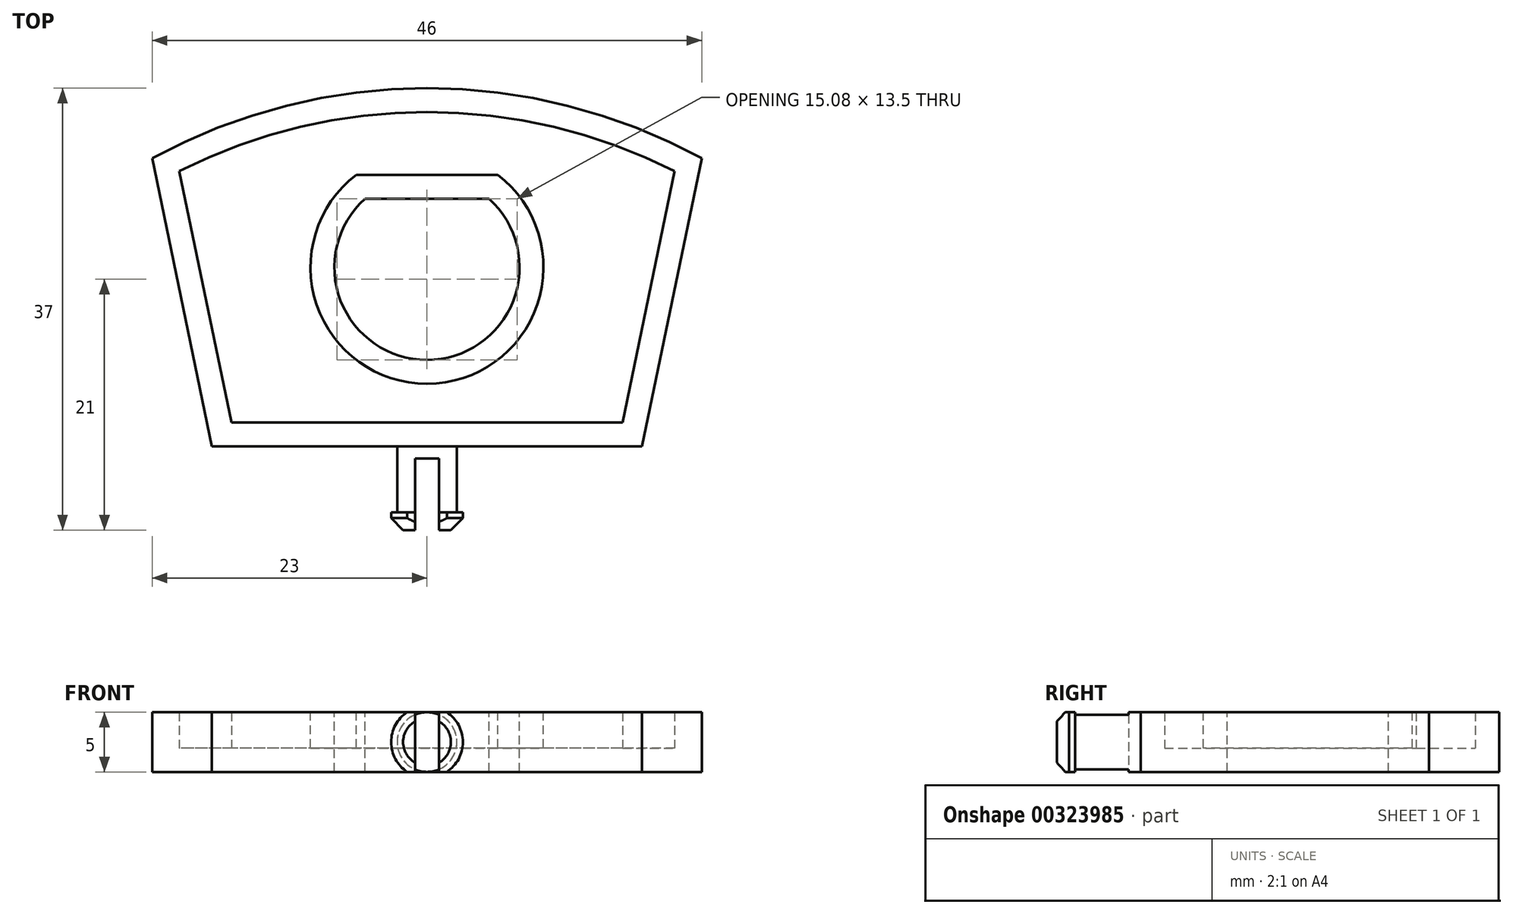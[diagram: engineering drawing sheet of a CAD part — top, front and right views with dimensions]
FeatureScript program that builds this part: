
annotation { "Feature Type Name" : "Feature", "Feature Type Description" : "" }
export const myFeature = defineFeature(function(context is Context, id is Id, definition is map)
    precondition{}
    {
        {
            var Q0;
            Q0=qCreatedBy(makeId("Top.planeOp"),FACE);
            var sketch = newSketch(context, id + "F0", { "sketchPlane" : qUnion([Q0])});
            skLineSegment(sketch, "E0", {"start": v(0, 0) * mm, "end": v(-18, 0) * mm});
            skLineSegment(sketch, "E1", {"start": v(-18, 0) * mm, "end": v(18, 0) * mm});
            skLineSegment(sketch, "E2", {"start": v(18, 0) * mm, "end": v(23, 24.13) * mm});
            skLineSegment(sketch, "E3", {"start": v(23, 24.13) * mm, "end": v(18, 0) * mm});
            skLineSegment(sketch, "E4", {"start": v(-18, 0) * mm, "end": v(-23, 24.13) * mm});
            skArc(sketch, "E5", {"start": v(23, 24.13) * mm, "mid": v(0, 30) * mm, "end": v(-23, 24.13) * mm});
            skSolve(sketch);
        }
        {
            var Q0;
            Q0 = qSketchRegion(id + "F0", true);
            extrude(context, id + "F1", {"entities" : qUnion([Q0]), "endBound" : BoundingType.SYMMETRIC, "depth" : 5 * mm});
        }
        {
            var Q0;
            Q0=makeQuery(id+"F1.opExtrude","CAP_FACE",FACE,{"disambiguationData":[OSD([sQuery(id+"F0.wireOp",EDGE,"E1"),sQuery(id+"F0.wireOp",EDGE,"E3"),sQuery(id+"F0.wireOp",EDGE,"E4"),sQuery(id+"F0.wireOp",EDGE,"E5")])],"isStart":false});
            var sketch = newSketch(context, id + "F2", { "sketchPlane" : qUnion([Q0])});
            skLineSegment(sketch, "E6", {"start": v(-5.2, 20.75) * mm, "end": v(5.2, 20.75) * mm});
            skArc(sketch, "E7", {"start": v(-5.2, 20.75) * mm, "mid": v(0, 7.25) * mm, "end": v(5.2, 20.75) * mm});
            skSolve(sketch);
        }
        {
            var Q0;
            Q0 = qSketchRegion(id + "F2", true);
            extrude(context, id + "F3", {"entities" : qUnion([Q0]), "operationType" : NewBodyOperationType.REMOVE, "endBound" : BoundingType.UP_TO_NEXT, "oppositeDirection" : true, "depth" : 25 * mm});
        }
        {
            var Q0;
            Q0=makeQuery(id+"F1.opExtrude","CAP_FACE",FACE,{"disambiguationData":[OSD([sQuery(id+"F0.wireOp",EDGE,"E1"),sQuery(id+"F0.wireOp",EDGE,"E3"),sQuery(id+"F0.wireOp",EDGE,"E4"),sQuery(id+"F0.wireOp",EDGE,"E5")])],"isStart":false});
            shell(context, id + "F4", {"entities" : qUnion([Q0]), "thickness" : 2 * mm});
        }
        {
            var Q0;
            Q0=qCreatedBy(makeId("Right.planeOp"),FACE);
            var sketch = newSketch(context, id + "F5", { "sketchPlane" : qUnion([Q0])});
            skLineSegment(sketch, "E8", {"start": v(0, 0) * mm, "end": v(-7, 0) * mm});
            skLineSegment(sketch, "E9", {"start": v(-7, 0) * mm, "end": v(-7, 3) * mm});
            skLineSegment(sketch, "E10", {"start": v(-7, 3) * mm, "end": v(-5.5, 3) * mm});
            skLineSegment(sketch, "E11", {"start": v(-5.5, 3) * mm, "end": v(-5.5, 2.5) * mm});
            skLineSegment(sketch, "E12", {"start": v(-5.5, 2.5) * mm, "end": v(0, 2.5) * mm});
            skLineSegment(sketch, "E13", {"start": v(0, 2.5) * mm, "end": v(0, 0) * mm});
            skSolve(sketch);
        }
        {
            var Q0;
            Q0 = qSketchRegion(id + "F5", true);
            var Q1;
            Q1=sQuery(id+"F5.wireOp",EDGE,"E8");
            revolve(context, id + "F6", {"operationType" : NewBodyOperationType.ADD, "entities" : qUnion([Q0]), "axis" : qUnion([Q1]), "revolveType" : RevolveType.FULL});
        }
        {
            var Q0;
            Q0=makeQuery(id+"F6.opRevolve","SWEPT_EDGE",EDGE,{"disambiguationData":[OSD([sQuery(id+"F5.wireOp",EDGE,"E9"),sQuery(id+"F5.wireOp",EDGE,"E10")])]});
            chamfer(context, id + "F7", {"entities" : qUnion([Q0]), "width" : 1 * mm, "tangentPropagation" : true});
        }
        {
            var Q0;
            Q0=makeQuery(id+"F6.opRevolve","SWEPT_FACE",FACE,{"disambiguationData":[OSD([sQuery(id+"F5.wireOp",EDGE,"E9")])]});
            var sketch = newSketch(context, id + "F8", { "sketchPlane" : qUnion([Q0])});
            skLineSegment(sketch, "E14.bottom", {"start": v(-23.45, 2.5) * mm, "end": v(23.74, 2.5) * mm});
            skLineSegment(sketch, "E14.top", {"start": v(-23.45, -2.5) * mm, "end": v(23.74, -2.5) * mm});
            skLineSegment(sketch, "E14.left", {"start": v(-23.45, 2.5) * mm, "end": v(-23.45, -2.5) * mm});
            skLineSegment(sketch, "E14.right", {"start": v(23.74, 2.5) * mm, "end": v(23.74, -2.5) * mm});
            skSolve(sketch);
        }
        {
            var Q0;
            Q0 = qSketchRegion(id + "F8", true);
            extrude(context, id + "F9", {"entities" : qUnion([Q0]), "operationType" : NewBodyOperationType.INTERSECT, "endBound" : BoundingType.THROUGH_ALL, "oppositeDirection" : true, "depth" : 25 * mm});
        }
        {
            var Q0;
            Q0=makeQuery(id+"F6.opRevolve","SWEPT_FACE",FACE,{"disambiguationData":[OSD([sQuery(id+"F5.wireOp",EDGE,"E9")])]});
            var sketch = newSketch(context, id + "F10", { "sketchPlane" : qUnion([Q0])});
            skLineSegment(sketch, "E15.bottom", {"start": v(-1, 3.53) * mm, "end": v(1, 3.53) * mm});
            skLineSegment(sketch, "E15.top", {"start": v(-1, -3.65) * mm, "end": v(1, -3.65) * mm});
            skLineSegment(sketch, "E15.left", {"start": v(-1, 3.53) * mm, "end": v(-1, -3.65) * mm});
            skLineSegment(sketch, "E15.right", {"start": v(1, 3.53) * mm, "end": v(1, -3.65) * mm});
            skSolve(sketch);
        }
        {
            var Q0;
            Q0 = qSketchRegion(id + "F10", true);
            extrude(context, id + "F11", {"entities" : qUnion([Q0]), "operationType" : NewBodyOperationType.REMOVE, "oppositeDirection" : true, "depth" : 6 * mm});
        }
    });
